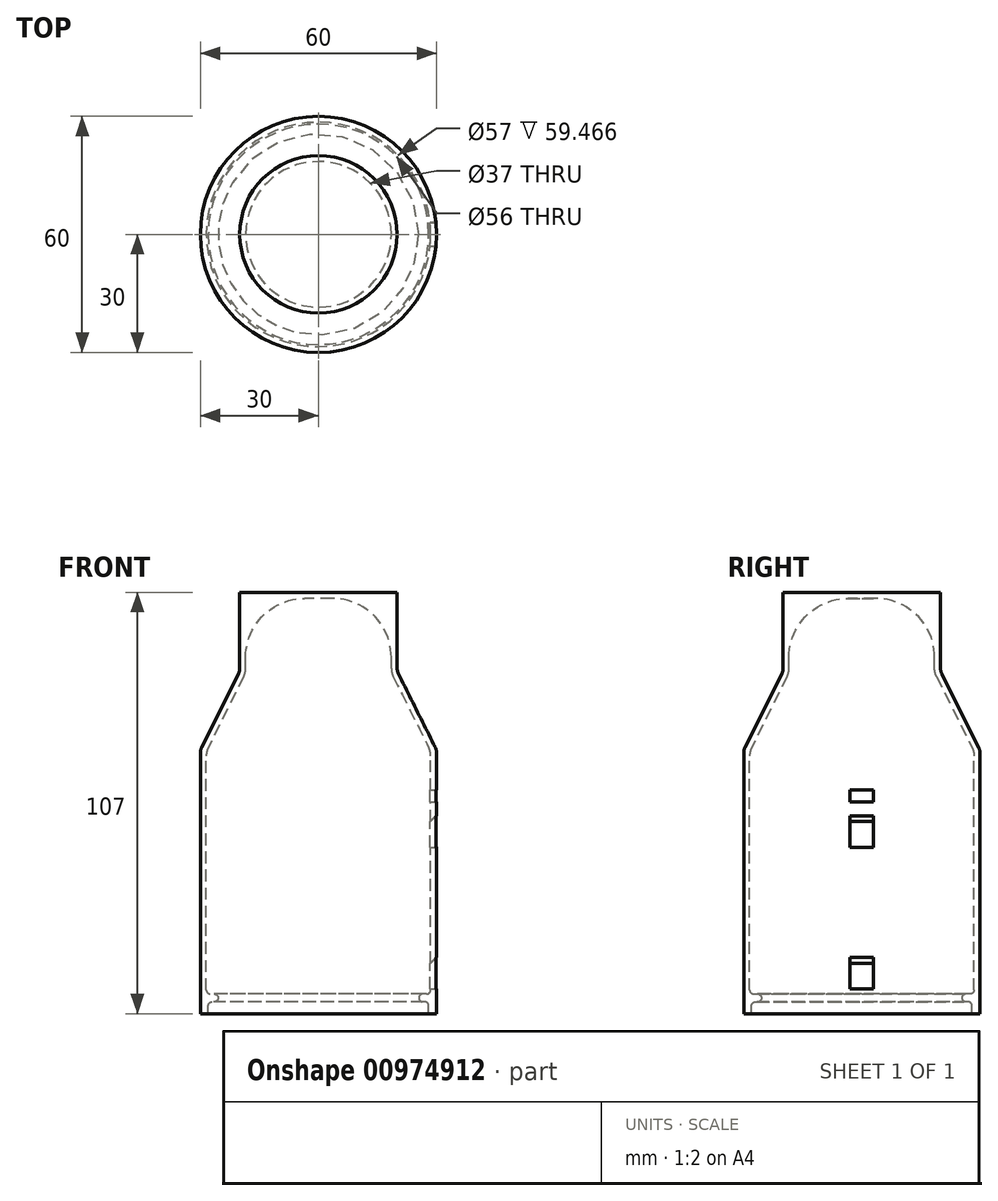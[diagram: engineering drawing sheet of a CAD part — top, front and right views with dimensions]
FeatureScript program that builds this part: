
annotation { "Feature Type Name" : "Feature", "Feature Type Description" : "" }
export const myFeature = defineFeature(function(context is Context, id is Id, definition is map)
    precondition{}
    {
        {
            var Q0;
            Q0=qCreatedBy(makeId("Front.planeOp"),FACE);
            var sketch = newSketch(context, id + "F0", { "sketchPlane" : qUnion([Q0])});
            skLineSegment(sketch, "E0", {"start": v(0, 0) * mm, "end": v(0, 66.3) * mm});
            skLineSegment(sketch, "E1", {"start": v(-9.68, 86.37) * mm, "end": v(-0.32, 67.63) * mm});
            skPoint(sketch, "E2.visualSharp", {"position": v(0, 67) * mm});
            skArc(sketch, "E2.filletArc", {"start": v(0, 66.3) * mm, "mid": v(-0.08, 66.98) * mm, "end": v(-0.32, 67.63) * mm});
            skLineSegment(sketch, "E3", {"start": v(-10, 87.7) * mm, "end": v(-10, 107) * mm});
            skLineSegment(sketch, "E4", {"start": v(-10, 107) * mm, "end": v(-30, 107) * mm});
            skPoint(sketch, "E5.visualSharp", {"position": v(-10, 87) * mm});
            skArc(sketch, "E5.filletArc", {"start": v(-10, 87.7) * mm, "mid": v(-9.92, 87.02) * mm, "end": v(-9.68, 86.37) * mm});
            skLineSegment(sketch, "E6.0", {"start": v(-26.5, 105.5) * mm, "end": v(-30, 105.5) * mm});
            skLineSegment(sketch, "E6.2", {"start": v(-11.02, 85.7) * mm, "end": v(-2.03, 67.7) * mm});
            skArc(sketch, "E6.3", {"start": v(-11.5, 87.7) * mm, "mid": v(-11.38, 86.67) * mm, "end": v(-11.02, 85.7) * mm});
            skLineSegment(sketch, "E6.4", {"start": v(-11.5, 87.7) * mm, "end": v(-11.5, 90.5) * mm});
            skLineSegment(sketch, "E7", {"start": v(-30, 107) * mm, "end": v(-30, 105.5) * mm});
            skPoint(sketch, "E8.visualSharp", {"position": v(-11.5, 105.5) * mm});
            skArc(sketch, "E8.filletArc", {"start": v(-11.5, 90.5) * mm, "mid": v(-15.9, 101.1) * mm, "end": v(-26.5, 105.5) * mm});
            skLineSegment(sketch, "E9", {"start": v(-3, 3) * mm, "end": v(-3.5, 3) * mm});
            skLineSegment(sketch, "E10", {"start": v(-4.5, 4) * mm, "end": v(-4.5, 4) * mm});
            skPoint(sketch, "E11.visualSharp", {"position": v(-4.5, 72.65) * mm});
            skPoint(sketch, "E12.visualSharp", {"position": v(-4.5, 3) * mm});
            skArc(sketch, "E13.filletArc", {"start": v(-4.5, 4) * mm, "mid": v(-4.2, 3.3) * mm, "end": v(-3.5, 3) * mm});
            skLineSegment(sketch, "E14.0", {"start": v(-1.5, 6) * mm, "end": v(-1.5, 65.47) * mm});
            skLineSegment(sketch, "E15.0", {"start": v(-2.5, 5) * mm, "end": v(-3.5, 5) * mm});
            skArc(sketch, "E16.filletArc", {"start": v(-1.5, 65.47) * mm, "mid": v(-1.63, 66.61) * mm, "end": v(-2.03, 67.7) * mm});
            skPoint(sketch, "E17.visualSharp", {"position": v(-4.5, 5) * mm});
            skArc(sketch, "E17.filletArc", {"start": v(-3.5, 5) * mm, "mid": v(-4.2, 4.7) * mm, "end": v(-4.5, 4) * mm});
            skPoint(sketch, "E18.visualSharp", {"position": v(-1.5, 5) * mm});
            skArc(sketch, "E18.filletArc", {"start": v(-2.5, 5) * mm, "mid": v(-1.8, 5.3) * mm, "end": v(-1.5, 6) * mm});
            skPoint(sketch, "E19.visualSharp", {"position": v(-2, 3) * mm});
            skArc(sketch, "E19.filletArc", {"start": v(-2, 2) * mm, "mid": v(-2.3, 2.7) * mm, "end": v(-3, 3) * mm});
            skLineSegment(sketch, "E20", {"start": v(-2, 2) * mm, "end": v(-2, 0.16) * mm});
            skLineSegment(sketch, "E21", {"start": v(-1.84, 0) * mm, "end": v(0, 0) * mm});
            skPoint(sketch, "E22.visualSharp", {"position": v(-2, 0) * mm});
            skArc(sketch, "E22.filletArc", {"start": v(-2, 0.16) * mm, "mid": v(-1.95, 0.05) * mm, "end": v(-1.84, 0) * mm});
            skSolve(sketch);
        }
        {
            var Q0;
            Q0=qSketchRegion(id+"F0",true);
            var Q1;
            Q1=sQuery(id+"F0.wireOp",EDGE,"E7");
            revolve(context, id + "F1", {"surfaceOperationType" : NewSurfaceOperationType.NEW, "entities" : qUnion([Q0]), "axis" : qUnion([Q1]), "revolveType" : RevolveType.FULL});
        }
        {
            var Q0;
            Q0=qCreatedBy(makeId("Right.planeOp"),FACE);
            var sketch = newSketch(context, id + "F2", { "sketchPlane" : qUnion([Q0])});
            skLineSegment(sketch, "E23.0", {"start": v(3, 6.3) * mm, "end": v(3, 12.3) * mm});
            skLineSegment(sketch, "E24.0", {"start": v(-3, 6.3) * mm, "end": v(-3, 12.3) * mm});
            skLineSegment(sketch, "E25", {"start": v(-3, 6.3) * mm, "end": v(3, 6.3) * mm});
            skLineSegment(sketch, "E26.0", {"start": v(-3, 12.3) * mm, "end": v(3, 12.3) * mm});
            skLineSegment(sketch, "E27.0", {"start": v(-3, 42.3) * mm, "end": v(3, 42.3) * mm});
            skLineSegment(sketch, "E28.0", {"start": v(-3, 48.3) * mm, "end": v(3, 48.3) * mm});
            skLineSegment(sketch, "E29.0", {"start": v(-3, 53.8) * mm, "end": v(3, 53.8) * mm});
            skLineSegment(sketch, "E30.0", {"start": v(-3, 56.8) * mm, "end": v(3, 56.8) * mm});
            skLineSegment(sketch, "E31.trimOffspring", {"start": v(-3, 42.3) * mm, "end": v(-3, 48.3) * mm});
            skLineSegment(sketch, "E32.trimOffspring", {"start": v(3, 42.3) * mm, "end": v(3, 48.3) * mm});
            skLineSegment(sketch, "E33.trimOffspring", {"start": v(-3, 53.8) * mm, "end": v(-3, 56.8) * mm});
            skLineSegment(sketch, "E34.trimOffspring", {"start": v(3, 53.8) * mm, "end": v(3, 56.8) * mm});
            skSolve(sketch);
        }
        {
            var Q0;
            Q0=qSketchRegion(id+"F2",true);
            extrude(context, id + "F3", {"entities" : qUnion([Q0]), "operationType" : NewBodyOperationType.REMOVE, "oppositeDirection" : true, "depth" : 25 * mm, "offsetDistance" : 25 * mm});
        }
        {
            var Q0;
            Q0=makeQuery(id+"F3.boolean.opBoolean","INTERSECT",EDGE,{"derivedFrom":[makeQuery(id+"F1.opRevolve","SWEPT_FACE",FACE,{"disambiguationData":[OSD([sQuery(id+"F0.wireOp",EDGE,"E0")])]}),makeQuery(id+"F3.opExtrude","SWEPT_FACE",FACE,{"disambiguationData":[OSD([sQuery(id+"F2.wireOp",EDGE,"E28.0")])]})]});
            var Q1;
            Q1=makeQuery(id+"F3.boolean.opBoolean","INTERSECT",EDGE,{"derivedFrom":[makeQuery(id+"F1.opRevolve","SWEPT_FACE",FACE,{"disambiguationData":[OSD([sQuery(id+"F0.wireOp",EDGE,"E0")])]}),makeQuery(id+"F3.opExtrude","SWEPT_FACE",FACE,{"disambiguationData":[OSD([sQuery(id+"F2.wireOp",EDGE,"E26.0")])]})]});
            chamfer(context, id + "F4", {"entities" : qUnion([Q0, Q1]), "width" : 2 * mm, "tangentPropagation" : true});
        }
    });
